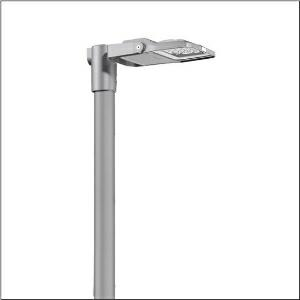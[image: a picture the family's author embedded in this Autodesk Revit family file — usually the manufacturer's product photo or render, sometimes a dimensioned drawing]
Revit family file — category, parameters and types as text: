
# Revit family: floodlight_fl_21_iq_micro___pl52_5xa7762a4d3a_1d61
name_source: partatom
category: Lighting Fixtures
units: mm (PartAtom-declared; Revit-internal decimal feet)

## family parameters
Cut with Voids When Loaded = No
Host = Face
Light Source = No
Part Type = Normal
Room Calculation Point = No
Round Connector Dimension = Use Diameter
Shared = No

## types (1)
- --- (1 x LED, 3010 lm, 23.1 W, 4000K)
    Apparent Load = 23 VA
    CIE Flux Codes = 26 60 98 100 100
    Color Rendering = 70
    Color Temperature = 4000K
    Default Elevation = 1800 mm
    Description = Floodlight FL 21 iQ micro, floodlight, primary light control with lens, of PMMA, primary optical cover: protective disc, of toughened safety glass, transparent, light distribution: PL52, light emission: direct distribution, installation type: surface-mounted, lamps: LED, High Power LED, rated values: 3.010lm | 23,1W | 130,3lm/W (begin service life); end service life: 3.010lm | 23,8W; at 50% lumin. flux: 1.505lm | 11W | 136,8lm/W, colour temperature: 4000K, colour rendering: CRI > 70, light colour: 740, light setting 1 begin service life: 100% | 3.010lm | 23,1W | 130,3lm/W | 4.000K, light setting 1 end service life: 23,8W, further light settings possible, control: Auto-Match, Temp-Guard, Night-Set, Smart-Wire, Desk-Remote (wireless, voltage-free reading and setting of iQ features in the workshop via application-optimized NFC function/RFID function), optimised constant luminous flux control (CLO 2.0), Street-Remote, pre-setting: linear dimming characteristic, with terminal, 6-pole, mains connection: 220..240V, AC, 50/60Hz, luminaire housing, of diecast aluminium, powder-coated, SITECO metallic grey (DB 702S), corrosivity category C5 mid according to DIN EN ISO 12944suitable for swimming poolschlorine-resistant, sealing non-destructively replaceable, please order mast flange separately, mast bracket, of steel, galvanised, powder-coated, SITECO metallic grey (DB 702S), protection rating (complete): IP66, insulation class (complete): insulation class II (safety insulation), certification: CE, ENEC, VDE, protection symbol: D, impact resistance: IK07, permissible operating ambient temperature: -40..+40°C, permissible operating ambient temperature for outdoor applications: -40..+50°C, standard: DIN EN 12944, LABS conformity tested according to VDMA 24364:2018-05, packaging unit: 1 piece

Light Distribution: PL52
    Height = 65 mm
    Lamp = 1 x LED
    Lamp Light Flux = 3010 lm
    Lamp Power = 23.1 W
    Lamp count = 1
    Length = 312 mm
    Luminous efficacy = 130 lm/W
    Manufacturer = Siteco
    ModVariant = No
    Model = 5XA7762A4D3A
    Number of Poles = 1
    OnlyDefault = Yes
    Power Factor = 1
    Product Name = Floodlight FL 21 iQ micro | PL52
    Product group = floodlight | pylon annexe
    ProductGroupID = 6201
    Protection Class = Protection class II
    Protection Degree = IP 66
    RLX_Detail_Level = 1
    RLX_Emergency_Light_Flux = 0 lm
    RLX_Emergency_Type = 0
    RLX_Emergency_Type_DB = No
    RlxData = <blob elided: 102257 chars, md5=75e64f44>
    Socket = socket
    Standby Power = 0 W
    System Light Flux = 3010 lm
    System Power = 23 W
    Type Comments = factory setting: luminous flux: 100 % | dim-lin: 254 | 455 mA
    Type Image = l_1007121.jpg
    URL = http://relux.com
    VarID = @adj_177219
    Voltage = 0 V
    Weight = 0.00 kg
    Width = 230 mm

## geometry (parser evidence)
native form markers: Blend x4, Sweep x11
no freeform markers — native parametric forms only
